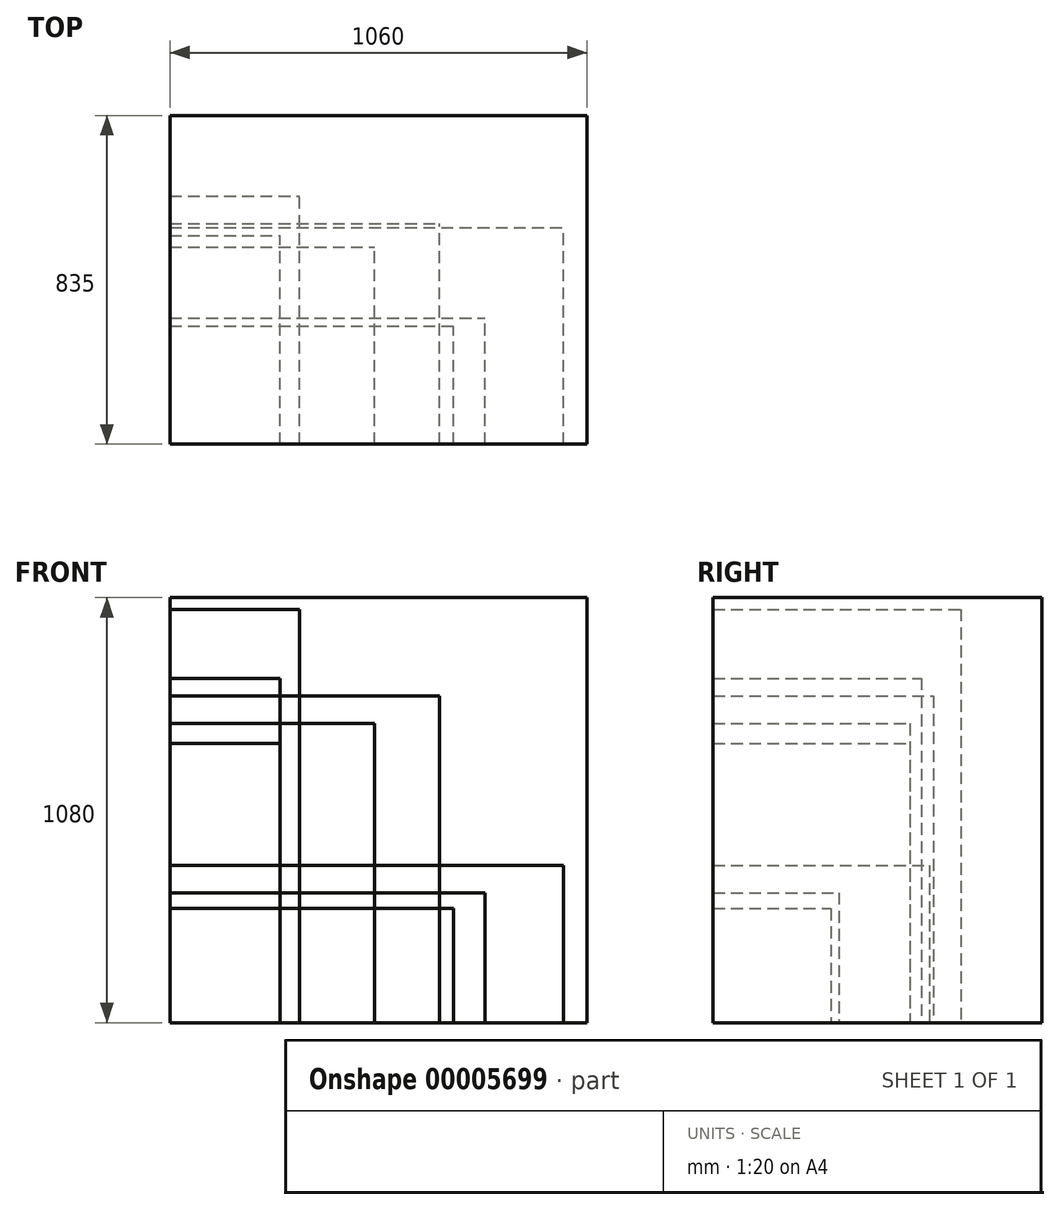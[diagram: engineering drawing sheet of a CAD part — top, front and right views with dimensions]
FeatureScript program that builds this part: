
annotation { "Feature Type Name" : "Feature", "Feature Type Description" : "" }
export const myFeature = defineFeature(function(context is Context, id is Id, definition is map)
    precondition{}
    {
        {
            var Q0;
            Q0=qCreatedBy(makeId("Top.planeOp"),FACE);
            var sketch = newSketch(context, id + "F0", { "sketchPlane" : qUnion([Q0])});
            skLineSegment(sketch, "E0.bottom", {"start": v(0, 0) * mm, "end": v(280, 0) * mm});
            skLineSegment(sketch, "E0.top", {"start": v(0, 500) * mm, "end": v(280, 500) * mm});
            skLineSegment(sketch, "E0.left", {"start": v(0, 0) * mm, "end": v(0, 500) * mm});
            skLineSegment(sketch, "E0.right", {"start": v(280, 0) * mm, "end": v(280, 500) * mm});
            skSolve(sketch);
        }
        {
            var Q0;
            Q0 = qSketchRegion(id + "F0", true);
            extrude(context, id + "F1", {"entities" : qUnion([Q0]), "depth" : 710 * mm});
        }
        {
            var Q0;
            Q0=qCreatedBy(makeId("Top.planeOp"),FACE);
            var sketch = newSketch(context, id + "F2", { "sketchPlane" : qUnion([Q0])});
            skLineSegment(sketch, "E1.bottom", {"start": v(0, 0) * mm, "end": v(280, 0) * mm});
            skLineSegment(sketch, "E1.top", {"start": v(0, 530) * mm, "end": v(280, 530) * mm});
            skLineSegment(sketch, "E1.left", {"start": v(0, 0) * mm, "end": v(0, 530) * mm});
            skLineSegment(sketch, "E1.right", {"start": v(280, 0) * mm, "end": v(280, 530) * mm});
            skSolve(sketch);
        }
        {
            var Q0;
            Q0 = qSketchRegion(id + "F2", true);
            extrude(context, id + "F3", {"entities" : qUnion([Q0]), "depth" : 875 * mm});
        }
        {
            var Q0;
            Q0=qCreatedBy(makeId("Top.planeOp"),FACE);
            var sketch = newSketch(context, id + "F4", { "sketchPlane" : qUnion([Q0])});
            skLineSegment(sketch, "E2.bottom", {"start": v(0, 0) * mm, "end": v(330, 0) * mm});
            skLineSegment(sketch, "E2.top", {"start": v(0, 630) * mm, "end": v(330, 630) * mm});
            skLineSegment(sketch, "E2.left", {"start": v(0, 0) * mm, "end": v(0, 630) * mm});
            skLineSegment(sketch, "E2.right", {"start": v(330, 0) * mm, "end": v(330, 630) * mm});
            skSolve(sketch);
        }
        {
            var Q0;
            Q0 = qSketchRegion(id + "F4", true);
            extrude(context, id + "F5", {"entities" : qUnion([Q0]), "depth" : 1050 * mm});
        }
        {
            var Q0;
            Q0=qCreatedBy(makeId("Top.planeOp"),FACE);
            var sketch = newSketch(context, id + "F6", { "sketchPlane" : qUnion([Q0])});
            skLineSegment(sketch, "E3.bottom", {"start": v(0, 0) * mm, "end": v(1000, 0) * mm});
            skLineSegment(sketch, "E3.top", {"start": v(0, 550) * mm, "end": v(1000, 550) * mm});
            skLineSegment(sketch, "E3.left", {"start": v(0, 0) * mm, "end": v(0, 550) * mm});
            skLineSegment(sketch, "E3.right", {"start": v(1000, 0) * mm, "end": v(1000, 550) * mm});
            skSolve(sketch);
        }
        {
            var Q0;
            Q0 = qSketchRegion(id + "F6", true);
            extrude(context, id + "F7", {"entities" : qUnion([Q0]), "depth" : 400 * mm});
        }
        {
            var Q0;
            Q0=qCreatedBy(makeId("Top.planeOp"),FACE);
            var sketch = newSketch(context, id + "F8", { "sketchPlane" : qUnion([Q0])});
            skLineSegment(sketch, "E4.bottom", {"start": v(0, 0) * mm, "end": v(720, 0) * mm});
            skLineSegment(sketch, "E4.top", {"start": v(0, 300) * mm, "end": v(720, 300) * mm});
            skLineSegment(sketch, "E4.left", {"start": v(0, 0) * mm, "end": v(0, 300) * mm});
            skLineSegment(sketch, "E4.right", {"start": v(720, 0) * mm, "end": v(720, 300) * mm});
            skSolve(sketch);
        }
        {
            var Q0;
            Q0 = qSketchRegion(id + "F8", true);
            extrude(context, id + "F9", {"entities" : qUnion([Q0]), "depth" : 290 * mm});
        }
        {
            var Q0;
            Q0=qCreatedBy(makeId("Top.planeOp"),FACE);
            var sketch = newSketch(context, id + "F10", { "sketchPlane" : qUnion([Q0])});
            skLineSegment(sketch, "E5.bottom", {"start": v(0, 0) * mm, "end": v(800, 0) * mm});
            skLineSegment(sketch, "E5.top", {"start": v(0, 320) * mm, "end": v(800, 320) * mm});
            skLineSegment(sketch, "E5.left", {"start": v(0, 0) * mm, "end": v(0, 320) * mm});
            skLineSegment(sketch, "E5.right", {"start": v(800, 0) * mm, "end": v(800, 320) * mm});
            skSolve(sketch);
        }
        {
            var Q0;
            Q0 = qSketchRegion(id + "F10", true);
            extrude(context, id + "F11", {"entities" : qUnion([Q0]), "depth" : 330 * mm});
        }
        {
            var Q0;
            Q0=qCreatedBy(makeId("Top.planeOp"),FACE);
            var sketch = newSketch(context, id + "F12", { "sketchPlane" : qUnion([Q0])});
            skLineSegment(sketch, "E6.bottom", {"start": v(0, 0) * mm, "end": v(685, 0) * mm});
            skLineSegment(sketch, "E6.top", {"start": v(0, 560) * mm, "end": v(685, 560) * mm});
            skLineSegment(sketch, "E6.left", {"start": v(0, 0) * mm, "end": v(0, 560) * mm});
            skLineSegment(sketch, "E6.right", {"start": v(685, 0) * mm, "end": v(685, 560) * mm});
            skSolve(sketch);
        }
        {
            var Q0;
            Q0 = qSketchRegion(id + "F12", true);
            extrude(context, id + "F13", {"entities" : qUnion([Q0]), "depth" : 830 * mm});
        }
        {
            var Q0;
            Q0=qCreatedBy(makeId("Top.planeOp"),FACE);
            var sketch = newSketch(context, id + "F14", { "sketchPlane" : qUnion([Q0])});
            skLineSegment(sketch, "E7.bottom", {"start": v(0, 0) * mm, "end": v(1060, 0) * mm});
            skLineSegment(sketch, "E7.top", {"start": v(0, 835) * mm, "end": v(1060, 835) * mm});
            skLineSegment(sketch, "E7.left", {"start": v(0, 0) * mm, "end": v(0, 835) * mm});
            skLineSegment(sketch, "E7.right", {"start": v(1060, 0) * mm, "end": v(1060, 835) * mm});
            skSolve(sketch);
        }
        {
            var Q0;
            Q0 = qSketchRegion(id + "F14", true);
            extrude(context, id + "F15", {"entities" : qUnion([Q0]), "depth" : 1080 * mm});
        }
        {
            var Q0;
            Q0=qCreatedBy(makeId("Top.planeOp"),FACE);
            var sketch = newSketch(context, id + "F16", { "sketchPlane" : qUnion([Q0])});
            skLineSegment(sketch, "E8.bottom", {"start": v(0, 0) * mm, "end": v(520, 0) * mm});
            skLineSegment(sketch, "E8.top", {"start": v(0, 500) * mm, "end": v(520, 500) * mm});
            skLineSegment(sketch, "E8.left", {"start": v(0, 0) * mm, "end": v(0, 500) * mm});
            skLineSegment(sketch, "E8.right", {"start": v(520, 0) * mm, "end": v(520, 500) * mm});
            skSolve(sketch);
        }
        {
            var Q0;
            Q0 = qSketchRegion(id + "F16", true);
            extrude(context, id + "F17", {"entities" : qUnion([Q0]), "depth" : 760 * mm});
        }
    });
